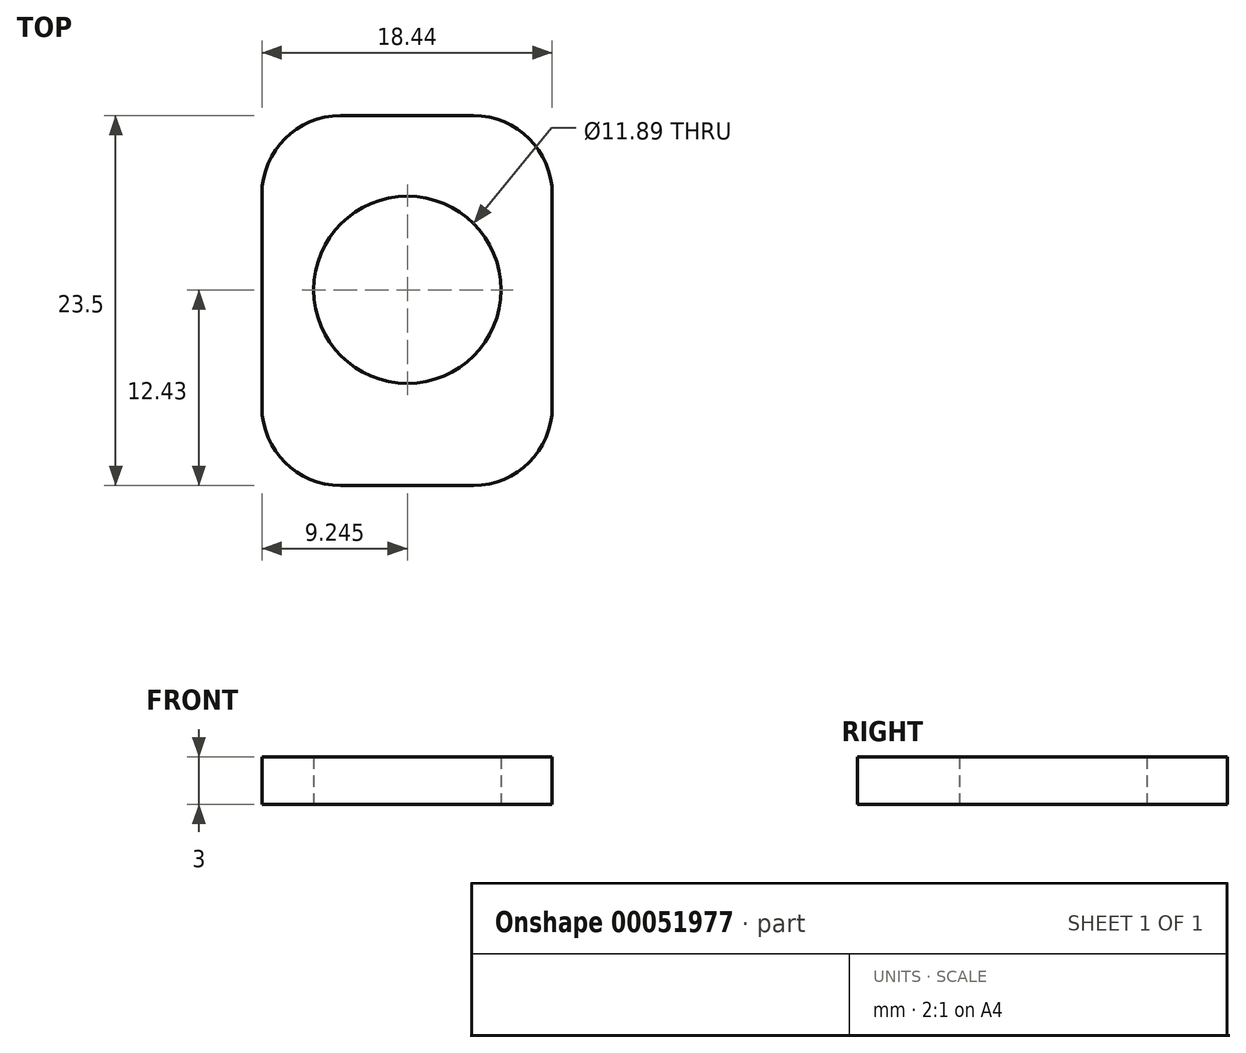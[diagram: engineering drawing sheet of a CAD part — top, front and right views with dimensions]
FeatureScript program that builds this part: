
annotation { "Feature Type Name" : "Feature", "Feature Type Description" : "" }
export const myFeature = defineFeature(function(context is Context, id is Id, definition is map)
    precondition{}
    {
        {
            var Q0;
            Q0=qCreatedBy(makeId("Top.planeOp"),FACE);
            var sketch = newSketch(context, id + "F0", { "sketchPlane" : qUnion([Q0])});
            skLineSegment(sketch, "E0.bottom", {"start": v(-40.27, 25.94) * mm, "end": v(-21.83, 25.94) * mm});
            skLineSegment(sketch, "E0.top", {"start": v(-40.27, 2.44) * mm, "end": v(-21.83, 2.44) * mm});
            skLineSegment(sketch, "E0.left", {"start": v(-40.27, 25.94) * mm, "end": v(-40.27, 2.44) * mm});
            skLineSegment(sketch, "E0.right", {"start": v(-21.83, 25.94) * mm, "end": v(-21.83, 2.44) * mm});
            skSolve(sketch);
        }
        {
            var Q0;
            Q0 = qSketchRegion(id + "F0", true);
            extrude(context, id + "F1", {"entities" : qUnion([Q0]), "depth" : 3 * mm});
        }
        {
            var Q0;
            Q0=makeQuery(id+"F1.opExtrude","SWEPT_EDGE",EDGE,{"disambiguationData":[OSD([sQuery(id+"F0.wireOp",EDGE,"E0.bottom"),sQuery(id+"F0.wireOp",EDGE,"E0.left")])]});
            var Q1;
            Q1=makeQuery(id+"F1.opExtrude","SWEPT_EDGE",EDGE,{"disambiguationData":[OSD([sQuery(id+"F0.wireOp",EDGE,"E0.bottom"),sQuery(id+"F0.wireOp",EDGE,"E0.right")])]});
            var Q2;
            Q2=makeQuery(id+"F1.opExtrude","SWEPT_EDGE",EDGE,{"disambiguationData":[OSD([sQuery(id+"F0.wireOp",EDGE,"E0.top"),sQuery(id+"F0.wireOp",EDGE,"E0.right")])]});
            var Q3;
            Q3=makeQuery(id+"F1.opExtrude","SWEPT_EDGE",EDGE,{"disambiguationData":[OSD([sQuery(id+"F0.wireOp",EDGE,"E0.top"),sQuery(id+"F0.wireOp",EDGE,"E0.left")])]});
            fillet(context, id + "F2", {"entities" : qUnion([Q0, Q1, Q2, Q3]), "radius" : 5 * mm, "tangentPropagation" : true, "allowEdgeOverflow" : false});
        }
        {
            var Q0;
            Q0=qCreatedBy(makeId("Top.planeOp"),FACE);
            var sketch = newSketch(context, id + "F3", { "sketchPlane" : qUnion([Q0])});
            skCircle(sketch, "E1", {"center": v(-31.03, 14.87) * mm, "radius": 5.95 * mm});
            skSolve(sketch);
        }
        {
            var Q0;
            Q0 = qSketchRegion(id + "F3", true);
            extrude(context, id + "F4", {"entities" : qUnion([Q0]), "operationType" : NewBodyOperationType.REMOVE, "depth" : 3 * mm});
        }
    });
